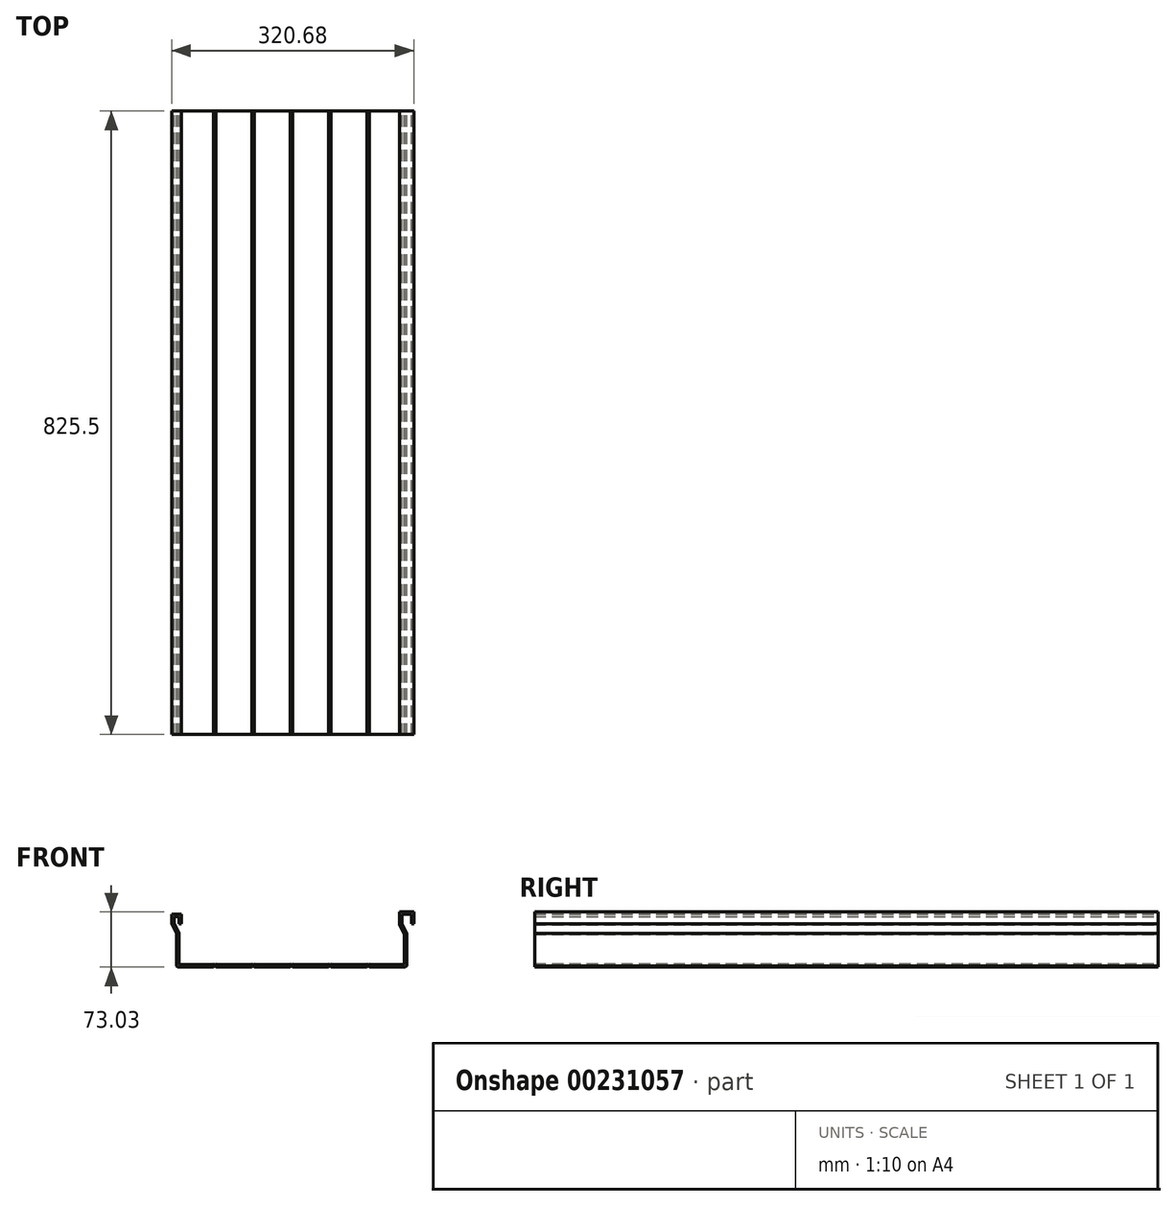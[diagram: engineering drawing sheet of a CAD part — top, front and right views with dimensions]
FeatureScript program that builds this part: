
annotation { "Feature Type Name" : "Feature", "Feature Type Description" : "" }
export const myFeature = defineFeature(function(context is Context, id is Id, definition is map)
    precondition{}
    {
        {
            var Q0;
            Q0=qCreatedBy(makeId("Front.planeOp"),FACE);
            var sketch = newSketch(context, id + "F0", { "sketchPlane" : qUnion([Q0])});
            skLineSegment(sketch, "E0", {"start": v(12.7, 57.15) * mm, "end": v(12.7, 69.85) * mm});
            skLineSegment(sketch, "E1", {"start": v(12.7, 69.85) * mm, "end": v(0, 69.85) * mm});
            skLineSegment(sketch, "E2", {"start": v(0, 69.85) * mm, "end": v(0, 57.15) * mm});
            skLineSegment(sketch, "E3", {"start": v(0, 57.15) * mm, "end": v(6.35, 44.45) * mm});
            skLineSegment(sketch, "E4", {"start": v(6.35, 44.45) * mm, "end": v(6.35, 1.59) * mm});
            skLineSegment(sketch, "E5", {"start": v(311.15, 1.59) * mm, "end": v(311.15, 44.45) * mm});
            skLineSegment(sketch, "E6", {"start": v(311.15, 44.45) * mm, "end": v(304.8, 57.15) * mm});
            skLineSegment(sketch, "E7", {"start": v(304.8, 57.15) * mm, "end": v(304.8, 69.85) * mm});
            skLineSegment(sketch, "E8", {"start": v(304.8, 69.85) * mm, "end": v(317.5, 69.85) * mm});
            skLineSegment(sketch, "E9", {"start": v(317.5, 69.85) * mm, "end": v(317.5, 57.15) * mm});
            skLineSegment(sketch, "E10.0", {"start": v(320.68, 73.03) * mm, "end": v(320.68, 57.15) * mm});
            skLineSegment(sketch, "E10.1", {"start": v(3.17, 57.9) * mm, "end": v(9.53, 45.2) * mm});
            skLineSegment(sketch, "E10.2", {"start": v(3.17, 66.68) * mm, "end": v(3.18, 57.9) * mm});
            skLineSegment(sketch, "E10.3", {"start": v(9.53, 66.68) * mm, "end": v(3.18, 66.68) * mm});
            skLineSegment(sketch, "E10.4", {"start": v(9.53, 57.15) * mm, "end": v(9.53, 66.68) * mm});
            skLineSegment(sketch, "E10.5", {"start": v(9.53, 45.2) * mm, "end": v(9.53, 3.18) * mm});
            skLineSegment(sketch, "E10.6", {"start": v(9.53, 3.18) * mm, "end": v(55.56, 3.18) * mm});
            skLineSegment(sketch, "E10.7", {"start": v(307.98, 3.18) * mm, "end": v(307.98, 43.7) * mm});
            skLineSegment(sketch, "E10.8", {"start": v(307.98, 43.7) * mm, "end": v(301.63, 56.4) * mm});
            skLineSegment(sketch, "E10.9", {"start": v(301.63, 56.4) * mm, "end": v(301.63, 73.03) * mm});
            skLineSegment(sketch, "E10.10", {"start": v(301.63, 73.03) * mm, "end": v(320.68, 73.03) * mm});
            skLineSegment(sketch, "E11", {"start": v(317.5, 57.15) * mm, "end": v(320.68, 57.15) * mm});
            skLineSegment(sketch, "E12", {"start": v(9.53, 57.15) * mm, "end": v(12.7, 57.15) * mm});
            skLineSegment(sketch, "E13", {"start": v(6.35, 1.59) * mm, "end": v(7.94, 0) * mm});
            skLineSegment(sketch, "E14", {"start": v(55.56, 0) * mm, "end": v(57.15, 1.59) * mm});
            skLineSegment(sketch, "E15", {"start": v(57.15, 1.59) * mm, "end": v(58.74, 0) * mm});
            skLineSegment(sketch, "E16.0.1.0", {"start": v(57.15, 4.76) * mm, "end": v(58.74, 3.18) * mm});
            skLineSegment(sketch, "E16.0.1.1", {"start": v(55.56, 3.17) * mm, "end": v(57.15, 4.76) * mm});
            skLineSegment(sketch, "E16.1.0.0", {"start": v(107.95, 1.59) * mm, "end": v(109.54, 0) * mm});
            skLineSegment(sketch, "E16.1.0.1", {"start": v(106.36, 0) * mm, "end": v(107.95, 1.59) * mm});
            skLineSegment(sketch, "E16.1.1.0", {"start": v(107.95, 4.76) * mm, "end": v(109.54, 3.18) * mm});
            skLineSegment(sketch, "E16.1.1.1", {"start": v(106.36, 3.17) * mm, "end": v(107.95, 4.76) * mm});
            skLineSegment(sketch, "E16.2.0.0", {"start": v(158.75, 1.59) * mm, "end": v(160.34, 0) * mm});
            skLineSegment(sketch, "E16.2.0.1", {"start": v(157.16, 0) * mm, "end": v(158.75, 1.59) * mm});
            skLineSegment(sketch, "E16.2.1.0", {"start": v(158.75, 4.76) * mm, "end": v(160.34, 3.18) * mm});
            skLineSegment(sketch, "E16.2.1.1", {"start": v(157.16, 3.18) * mm, "end": v(158.75, 4.76) * mm});
            skLineSegment(sketch, "E16.3.0.0", {"start": v(209.55, 1.59) * mm, "end": v(211.14, 0) * mm});
            skLineSegment(sketch, "E16.3.0.1", {"start": v(207.96, 0) * mm, "end": v(209.55, 1.59) * mm});
            skLineSegment(sketch, "E16.3.1.0", {"start": v(209.55, 4.76) * mm, "end": v(211.14, 3.17) * mm});
            skLineSegment(sketch, "E16.3.1.1", {"start": v(207.96, 3.18) * mm, "end": v(209.55, 4.76) * mm});
            skLineSegment(sketch, "E16.4.0.0", {"start": v(260.35, 1.59) * mm, "end": v(261.94, 0) * mm});
            skLineSegment(sketch, "E16.4.0.1", {"start": v(258.76, 0) * mm, "end": v(260.35, 1.59) * mm});
            skLineSegment(sketch, "E16.4.1.0", {"start": v(260.35, 4.76) * mm, "end": v(261.94, 3.17) * mm});
            skLineSegment(sketch, "E16.4.1.1", {"start": v(258.76, 3.18) * mm, "end": v(260.35, 4.76) * mm});
            skLineSegment(sketch, "E17", {"start": v(7.94, 0) * mm, "end": v(55.56, 0) * mm});
            skLineSegment(sketch, "E18", {"start": v(58.74, 0) * mm, "end": v(106.36, 0) * mm});
            skLineSegment(sketch, "E19", {"start": v(109.54, 0) * mm, "end": v(157.16, 0) * mm});
            skLineSegment(sketch, "E20", {"start": v(160.34, 0) * mm, "end": v(207.96, 0) * mm});
            skLineSegment(sketch, "E21", {"start": v(211.14, 0) * mm, "end": v(258.76, 0) * mm});
            skLineSegment(sketch, "E22", {"start": v(261.94, 0) * mm, "end": v(309.56, 0) * mm});
            skLineSegment(sketch, "E23.trimOffspring", {"start": v(261.94, 3.18) * mm, "end": v(307.98, 3.18) * mm});
            skLineSegment(sketch, "E24.trimOffspring", {"start": v(211.14, 3.18) * mm, "end": v(258.76, 3.18) * mm});
            skLineSegment(sketch, "E25.trimOffspring", {"start": v(160.34, 3.18) * mm, "end": v(207.96, 3.18) * mm});
            skLineSegment(sketch, "E26.trimOffspring", {"start": v(109.54, 3.18) * mm, "end": v(157.16, 3.18) * mm});
            skLineSegment(sketch, "E27.trimOffspring", {"start": v(58.74, 3.18) * mm, "end": v(106.36, 3.18) * mm});
            skLineSegment(sketch, "E28", {"start": v(311.15, 1.59) * mm, "end": v(309.56, 0) * mm});
            skSolve(sketch);
        }
        {
            var Q0;
            Q0=qSketchRegion(id+"F0",true);
            extrude(context, id + "F1", {"entities" : qUnion([Q0]), "depth" : 825.5 * mm});
        }
    });
